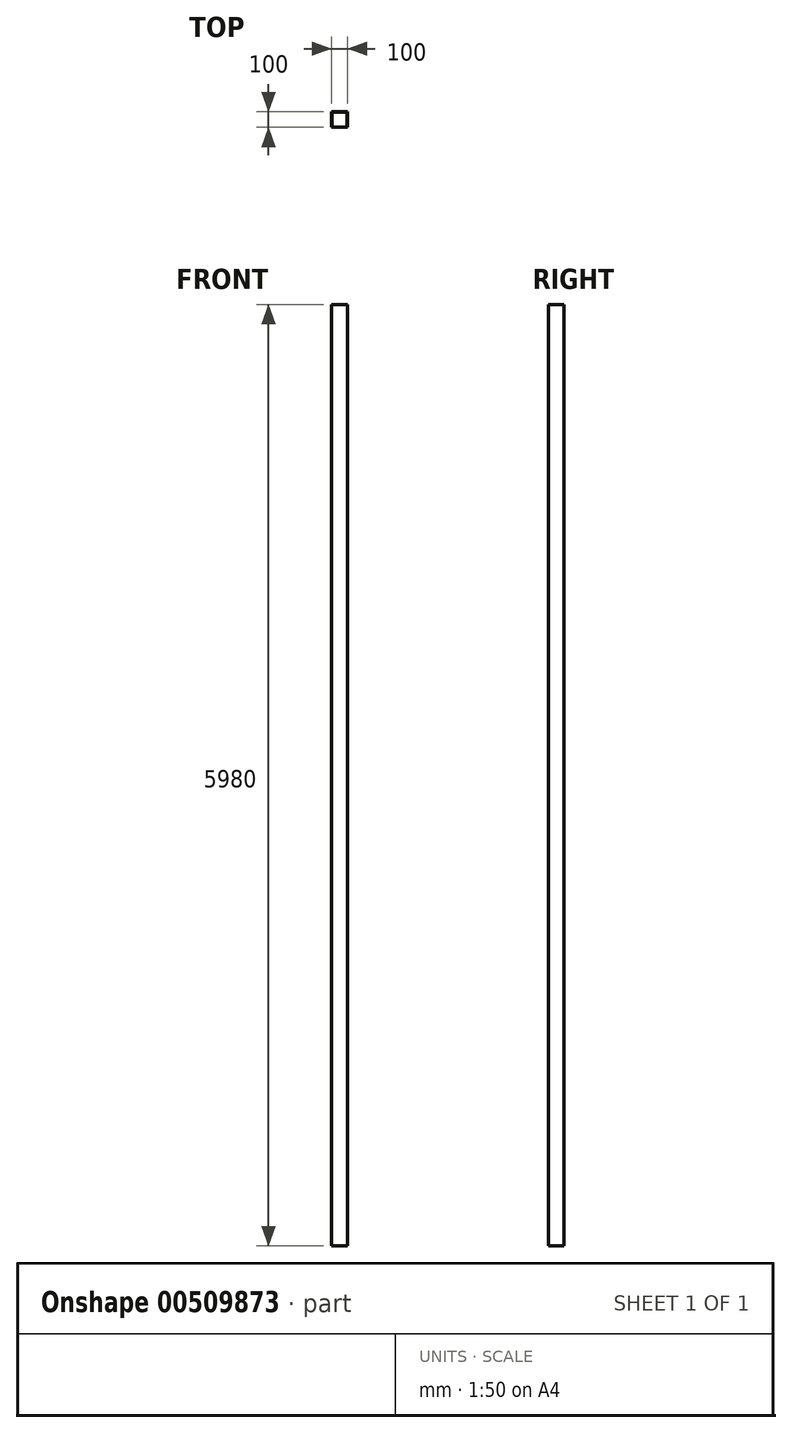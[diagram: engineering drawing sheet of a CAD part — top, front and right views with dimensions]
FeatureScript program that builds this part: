
annotation { "Feature Type Name" : "Feature", "Feature Type Description" : "" }
export const myFeature = defineFeature(function(context is Context, id is Id, definition is map)
    precondition{}
    {
        {
            var Q0;
            Q0=qCreatedBy(makeId("Top.planeOp"),FACE);
            var sketch = newSketch(context, id + "F0", { "sketchPlane" : qUnion([Q0])});
            skLineSegment(sketch, "E0.bottom", {"start": v(50, -50) * mm, "end": v(-50, -50) * mm});
            skLineSegment(sketch, "E0.top", {"start": v(50, 50) * mm, "end": v(-50, 50) * mm});
            skLineSegment(sketch, "E0.left", {"start": v(50, -50) * mm, "end": v(50, 50) * mm});
            skLineSegment(sketch, "E0.right", {"start": v(-50, -50) * mm, "end": v(-50, 50) * mm});
            skPoint(sketch, "E0.middle", {"position": v(0, 0) * mm});
            skLineSegment(sketch, "E1.bottom", {"start": v(47, -47) * mm, "end": v(-47, -47) * mm});
            skLineSegment(sketch, "E1.top", {"start": v(47, 47) * mm, "end": v(-47, 47) * mm});
            skLineSegment(sketch, "E1.left", {"start": v(47, -47) * mm, "end": v(47, 47) * mm});
            skLineSegment(sketch, "E1.right", {"start": v(-47, -47) * mm, "end": v(-47, 47) * mm});
            skSolve(sketch);
        }
        {
            var Q0;
            Q0=sQuery(id+"F0.wireOp",EDGE,"E0.right");
            var Q1;
            Q1=sQuery(id+"F0.wireOp",EDGE,"E1.right");
            var Q2;
            Q2=sQuery(id+"F0.wireOp",EDGE,"E0.top");
            var Q3;
            Q3=sQuery(id+"F0.wireOp",EDGE,"E1.top");
            var Q4;
            Q4=sQuery(id+"F0.wireOp",EDGE,"E0.left");
            var Q5;
            Q5=sQuery(id+"F0.wireOp",EDGE,"E1.left");
            var Q6;
            Q6=sQuery(id+"F0.wireOp",EDGE,"E1.bottom");
            var Q7;
            Q7=sQuery(id+"F0.wireOp",EDGE,"E0.bottom");
            extrude(context, id + "F1", {"bodyType" : ToolBodyType.SURFACE, "surfaceEntities" : qUnion([Q0, Q1, Q2, Q3, Q4, Q5, Q6, Q7]), "depth" : 5980 * mm});
        }
    });
